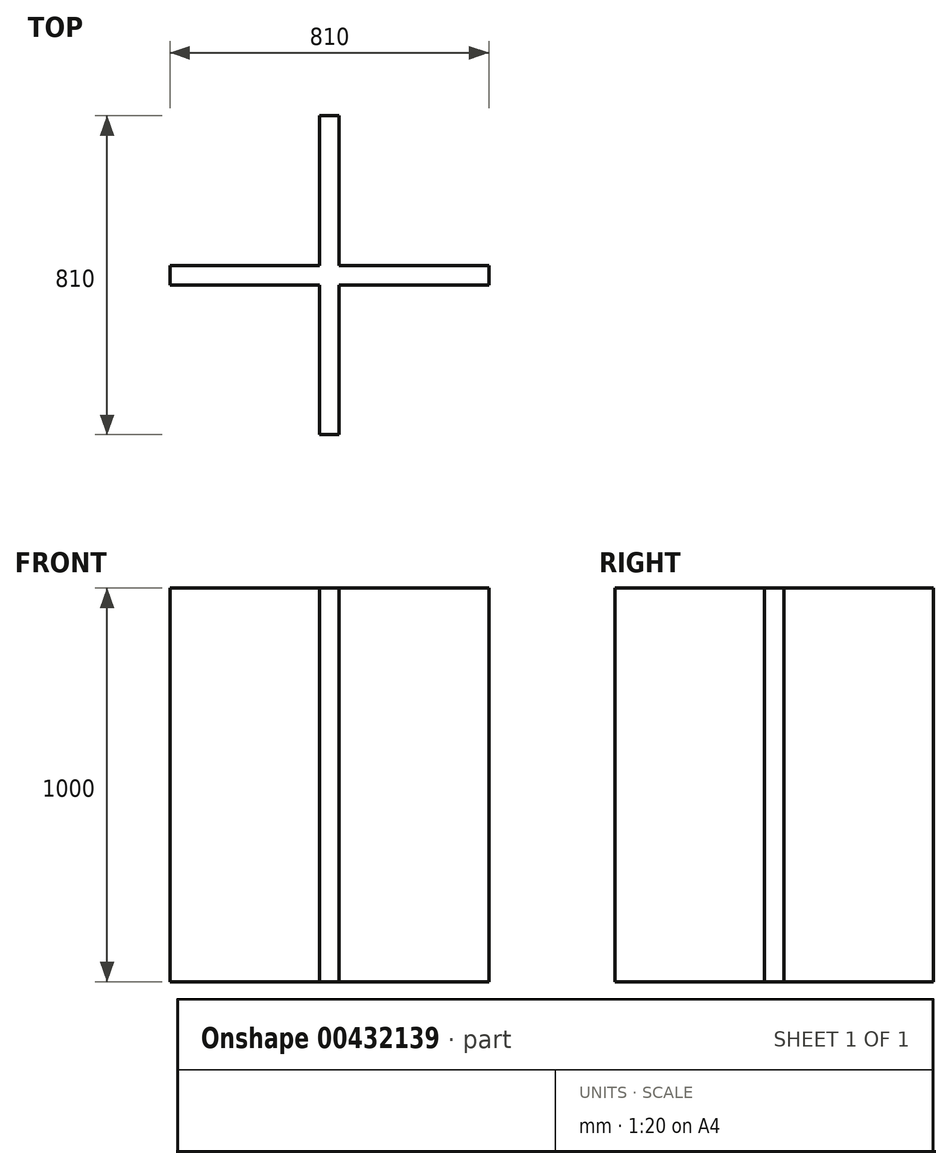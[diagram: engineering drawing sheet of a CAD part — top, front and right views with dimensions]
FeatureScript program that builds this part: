
annotation { "Feature Type Name" : "Feature", "Feature Type Description" : "" }
export const myFeature = defineFeature(function(context is Context, id is Id, definition is map)
    precondition{}
    {
        {
            var Q0;
            Q0=qCreatedBy(makeId("Top.planeOp"),FACE);
            var sketch = newSketch(context, id + "F0", { "sketchPlane" : qUnion([Q0])});
            skLineSegment(sketch, "E0.bottom", {"start": v(-406.73, -1.02) * mm, "end": v(403.27, -1.02) * mm});
            skLineSegment(sketch, "E0.top", {"start": v(-406.73, -51.02) * mm, "end": v(403.27, -51.02) * mm});
            skLineSegment(sketch, "E0.left", {"start": v(-406.73, -1.02) * mm, "end": v(-406.73, -51.02) * mm});
            skLineSegment(sketch, "E0.right", {"start": v(403.27, -1.02) * mm, "end": v(403.27, -51.02) * mm});
            skLineSegment(sketch, "E1.bottom", {"start": v(-26.73, -1.02) * mm, "end": v(23.27, -1.02) * mm});
            skLineSegment(sketch, "E1.top", {"start": v(-26.73, -51.02) * mm, "end": v(23.27, -51.02) * mm});
            skLineSegment(sketch, "E1.left", {"start": v(-26.73, -1.02) * mm, "end": v(-26.73, -51.02) * mm});
            skLineSegment(sketch, "E1.right", {"start": v(23.27, -1.02) * mm, "end": v(23.27, -51.02) * mm});
            skLineSegment(sketch, "E2.bottom", {"start": v(-26.73, 378.98) * mm, "end": v(23.27, 378.98) * mm});
            skLineSegment(sketch, "E2.top", {"start": v(-26.73, -431.02) * mm, "end": v(23.27, -431.02) * mm});
            skLineSegment(sketch, "E2.left", {"start": v(-26.73, 378.98) * mm, "end": v(-26.73, -431.02) * mm});
            skLineSegment(sketch, "E2.right", {"start": v(23.27, 378.98) * mm, "end": v(23.27, -431.02) * mm});
            skLineSegment(sketch, "E3.bottom", {"start": v(0, -51.02) * mm, "end": v(23.27, -51.02) * mm});
            skLineSegment(sketch, "E3.top", {"start": v(0, -51.02) * mm, "end": v(23.27, -51.02) * mm});
            skLineSegment(sketch, "E3.left", {"start": v(0, -51.02) * mm, "end": v(0, -51.02) * mm});
            skLineSegment(sketch, "E3.right", {"start": v(23.27, -51.02) * mm, "end": v(23.27, -51.02) * mm});
            skSolve(sketch);
        }
        {
            var Q0;
            {var subQ0=sQuery(id+"F0.wireOp",EDGE,"E1.left");var subQ1=makeQuery(id+"F0.imprint","IMPRINT",EDGE,{"derivedFrom":subQ0});var subQ16=sQuery(id+"F0.wireOp",EDGE,"E2.top");var subQ17=sQuery(id+"F0.wireOp",EDGE,"E2.bottom");var subQ18=sQuery(id+"F0.wireOp",EDGE,"E0.right");var subQ19=sQuery(id+"F0.wireOp",EDGE,"E0.left");Q0=qUnion([makeQuery(id+"F0.imprint","IMPRINT",FACE,{"disambiguationData":[TD([[makeQuery(id+"F0.imprint","IMPRINT",EDGE,{"derivedFrom":subQ19}),1.0]])]}),makeQuery(id+"F0.imprint","IMPRINT",FACE,{"disambiguationData":[TD([[makeQuery(id+"F0.imprint","IMPRINT",EDGE,{"derivedFrom":subQ18}),-1.0]])]}),makeQuery(id+"F0.imprint","IMPRINT",FACE,{"disambiguationData":[TD([[makeQuery(id+"F0.imprint","IMPRINT",EDGE,{"derivedFrom":subQ17}),-1.0]])]}),makeQuery(id+"F0.imprint","IMPRINT",FACE,{"disambiguationData":[TD([[makeQuery(id+"F0.imprint","IMPRINT",EDGE,{"derivedFrom":subQ16}),1.0]])]}),makeQuery(id+"F0.imprint","IMPRINT",FACE,{"disambiguationData":[TD([[subQ1,1.0]])]})]);}
            extrude(context, id + "F1", {"entities" : qUnion([Q0]), "depth" : 1000 * mm});
        }
    });
